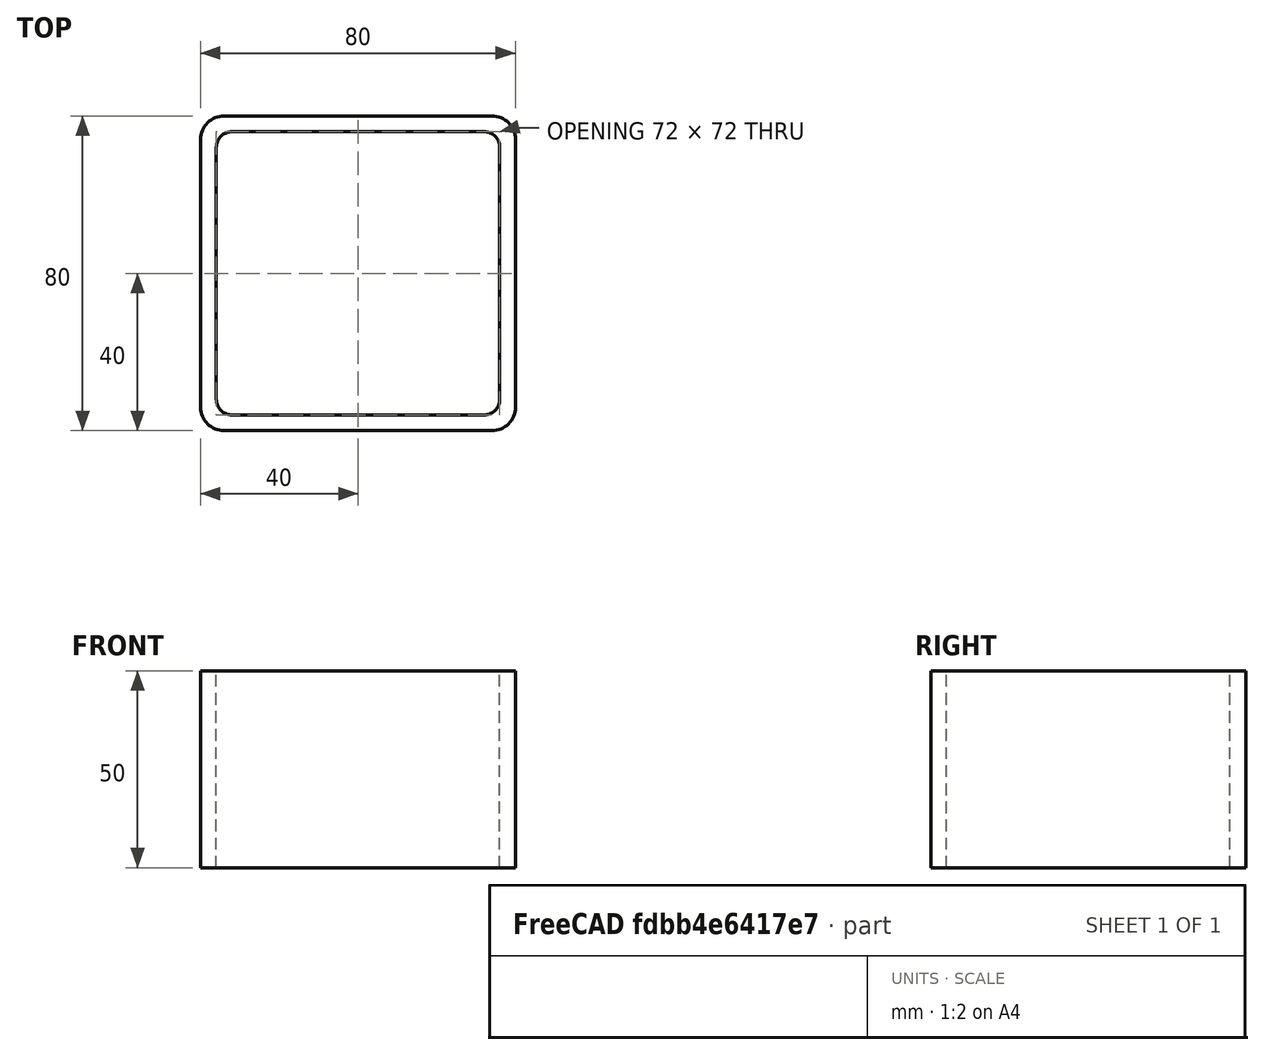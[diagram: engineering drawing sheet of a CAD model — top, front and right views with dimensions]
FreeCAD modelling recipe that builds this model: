
FCSTD DOCUMENT  (FreeCAD 0.15R4671 (Git))
Label: Square hollow section 80x80x4 EN10219 S235JRH
License: All rights reserved
LicenseURL: http://en.wikipedia.org/wiki/All_rights_reserved
objects: Sketcher::SketchObject×1, Part::Extrusion×1
note: 2 computed .brp shape members not serialized (recipe doc carries the construction recipe); baked Part::Feature solids carry a one-line shape summary decoded from their .brp

FEATURE [Sketcher::SketchObject] Sketch
  sketch-geometry (16):
    g0: LineSegment StartX=-32 StartY=36 StartZ=0 EndX=32 EndY=36 EndZ=0
    g1: LineSegment StartX=36 StartY=32 StartZ=0 EndX=36 EndY=-32 EndZ=0
    g2: LineSegment StartX=32 StartY=-36 StartZ=0 EndX=-32 EndY=-36 EndZ=0
    g3: LineSegment StartX=-36 StartY=-32 StartZ=0 EndX=-36 EndY=32 EndZ=0
    g4: LineSegment StartX=-34 StartY=40 StartZ=0 EndX=34 EndY=40 EndZ=0
    g5: LineSegment StartX=40 StartY=34 StartZ=0 EndX=40 EndY=-34 EndZ=0
    g6: LineSegment StartX=34 StartY=-40 StartZ=0 EndX=-34 EndY=-40 EndZ=0
    g7: LineSegment StartX=-40 StartY=-34 StartZ=0 EndX=-40 EndY=34 EndZ=0
    g8: ArcOfCircle CenterX=-32 CenterY=32 CenterZ=0 NormalX=0 NormalY=0 NormalZ=1 Radius=4 StartAngle=1.5708 EndAngle=3.14159
    g9: ArcOfCircle CenterX=32 CenterY=32 CenterZ=0 NormalX=0 NormalY=0 NormalZ=1 Radius=4 StartAngle=0 EndAngle=1.5708
    g10: ArcOfCircle CenterX=32 CenterY=-32 CenterZ=0 NormalX=0 NormalY=0 NormalZ=1 Radius=4 StartAngle=4.71239 EndAngle=6.28319
    g11: ArcOfCircle CenterX=-32 CenterY=-32 CenterZ=0 NormalX=0 NormalY=0 NormalZ=1 Radius=4 StartAngle=3.14159 EndAngle=4.71239
    g12: ArcOfCircle CenterX=34 CenterY=34 CenterZ=0 NormalX=0 NormalY=0 NormalZ=1 Radius=6 StartAngle=0 EndAngle=1.5708
    g13: ArcOfCircle CenterX=34 CenterY=-34 CenterZ=0 NormalX=0 NormalY=0 NormalZ=1 Radius=6 StartAngle=4.71239 EndAngle=6.28319
    g14: ArcOfCircle CenterX=-34 CenterY=-34 CenterZ=0 NormalX=0 NormalY=0 NormalZ=1 Radius=6 StartAngle=3.14159 EndAngle=4.71239
    g15: ArcOfCircle CenterX=-34 CenterY=34 CenterZ=0 NormalX=0 NormalY=0 NormalZ=1 Radius=6 StartAngle=1.5708 EndAngle=3.14159
  constraints (36):
    c: Horizontal(g2)
    c: Vertical(g3)
    c: Horizontal(g6)
    c: Vertical(g7)
    c: Tangent(g3,g8) = 1.5708
    c: Tangent(g0,g8) = 1.5708
    c: Tangent(g0,g9) = 1.5708
    c: Tangent(g1,g9) = 1.5708
    c: Tangent(g1,g10) = 1.5708
    c: Tangent(g2,g10) = 1.5708
    c: Tangent(g2,g11) = 1.5708
    c: Tangent(g3,g11) = 1.5708
    c: Tangent(g4,g12) = 1.5708
    c: Tangent(g5,g12) = 1.5708
    c: Tangent(g5,g13) = 1.5708
    c: Tangent(g6,g13) = 1.5708
    c: Tangent(g6,g14) = 1.5708
    c: Tangent(g7,g14) = 1.5708
    c: Tangent(g7,g15) = 1.5708
    c: Tangent(g4,g15) = 1.5708
    c: Equal(g9,g8)
    c: Equal(g9,g11)
    c: Equal(g9,g10)
    c: Equal(g12,g15)
    c: Equal(g12,g14)
    c: Equal(g12,g13)
    c: Symmetric(g4,g6,g-1)
    c: Symmetric(g7,g5,g-2)
    c: DistanceY(g4,g6) = -80
    c: DistanceX(g7,g5) = 80
    c: Symmetric(g3,g1,g-2)
    c: Symmetric(g0,g2,g-1)
    c: DistanceY(g0,g4) = 4
    c: DistanceX(g5,g1) = -4
    c: Radius(g9) = 4
    c: Radius(g12) = 6
FEATURE [Part::Extrusion] Extrude  label="Square hollow section 80x80x4 EN10219 S235JRH"
  Base = -> Sketch
  Dir = (0,0,50)
  Solid = true
